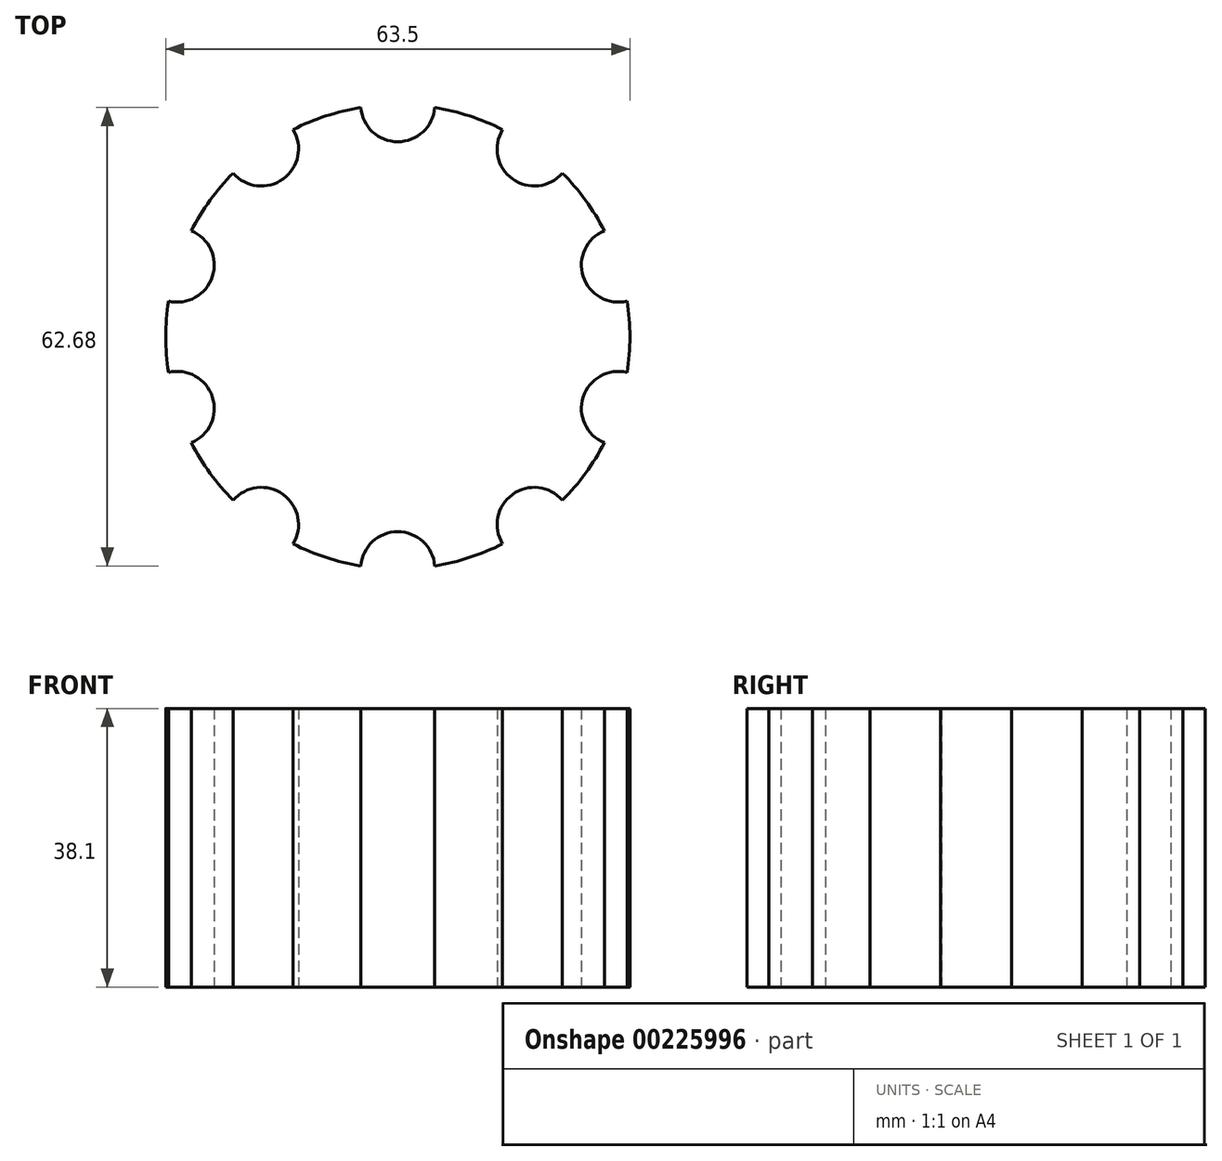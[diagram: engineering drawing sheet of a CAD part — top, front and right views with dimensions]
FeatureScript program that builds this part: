
annotation { "Feature Type Name" : "Feature", "Feature Type Description" : "" }
export const myFeature = defineFeature(function(context is Context, id is Id, definition is map)
    precondition{}
    {
        {
            var Q0;
            Q0=qCreatedBy(makeId("Top.planeOp"),FACE);
            var sketch = newSketch(context, id + "F0", { "sketchPlane" : qUnion([Q0])});
            skCircle(sketch, "E0", {"center": v(0, 0) * mm, "radius": 31.75 * mm});
            skSolve(sketch);
        }
        {
            var Q0;
            Q0=qSketchRegion(id+"F0",true);
            extrude(context, id + "F1", {"entities" : qUnion([Q0]), "depth" : 38.1 * mm});
        }
        {
            var Q0;
            Q0=qCreatedBy(makeId("Top.planeOp"),FACE);
            var sketch = newSketch(context, id + "F2", { "sketchPlane" : qUnion([Q0])});
            skCircle(sketch, "E1", {"center": v(0, 31.75) * mm, "radius": 5.08 * mm});
            skCircle(sketch, "E2.1.0", {"center": v(-18.66, 25.69) * mm, "radius": 5.08 * mm});
            skCircle(sketch, "E2.2.0", {"center": v(-30.2, 9.81) * mm, "radius": 5.08 * mm});
            skCircle(sketch, "E2.3.0", {"center": v(-30.2, -9.81) * mm, "radius": 5.08 * mm});
            skCircle(sketch, "E2.4.0", {"center": v(-18.66, -25.69) * mm, "radius": 5.08 * mm});
            skCircle(sketch, "E2.5.0", {"center": v(0, -31.75) * mm, "radius": 5.08 * mm});
            skCircle(sketch, "E2.6.0", {"center": v(18.66, -25.69) * mm, "radius": 5.08 * mm});
            skCircle(sketch, "E2.7.0", {"center": v(30.2, -9.81) * mm, "radius": 5.08 * mm});
            skCircle(sketch, "E2.8.0", {"center": v(30.2, 9.81) * mm, "radius": 5.08 * mm});
            skCircle(sketch, "E2.9.0", {"center": v(18.66, 25.69) * mm, "radius": 5.08 * mm});
            skPoint(sketch, "E2.center", {"position": v(0, 0) * mm});
            skSolve(sketch);
        }
        {
            var Q0;
            Q0=qSketchRegion(id+"F2",true);
            extrude(context, id + "F3", {"entities" : qUnion([Q0]), "depth" : 50.8 * mm});
        }
        {
            var Q0;
            Q0=makeQuery(id+"F3.opExtrude","SWEPT_BODY",BODY,{"disambiguationData":[OSD([sQuery(id+"F2.wireOp",EDGE,"E2.2.0")])]});
            var Q1;
            Q1=makeQuery(id+"F3.opExtrude","SWEPT_BODY",BODY,{"disambiguationData":[OSD([sQuery(id+"F2.wireOp",EDGE,"E2.3.0")])]});
            var Q2;
            Q2=makeQuery(id+"F3.opExtrude","SWEPT_BODY",BODY,{"disambiguationData":[OSD([sQuery(id+"F2.wireOp",EDGE,"E2.4.0")])]});
            var Q3;
            Q3=makeQuery(id+"F3.opExtrude","SWEPT_BODY",BODY,{"disambiguationData":[OSD([sQuery(id+"F2.wireOp",EDGE,"E2.5.0")])]});
            var Q4;
            Q4=makeQuery(id+"F3.opExtrude","SWEPT_BODY",BODY,{"disambiguationData":[OSD([sQuery(id+"F2.wireOp",EDGE,"E2.6.0")])]});
            var Q5;
            Q5=makeQuery(id+"F3.opExtrude","SWEPT_BODY",BODY,{"disambiguationData":[OSD([sQuery(id+"F2.wireOp",EDGE,"E2.7.0")])]});
            var Q6;
            Q6=makeQuery(id+"F3.opExtrude","SWEPT_BODY",BODY,{"disambiguationData":[OSD([sQuery(id+"F2.wireOp",EDGE,"E2.8.0")])]});
            var Q7;
            Q7=makeQuery(id+"F3.opExtrude","SWEPT_BODY",BODY,{"disambiguationData":[OSD([sQuery(id+"F2.wireOp",EDGE,"E2.9.0")])]});
            var Q8;
            Q8=makeQuery(id+"F3.opExtrude","SWEPT_BODY",BODY,{"disambiguationData":[OSD([sQuery(id+"F2.wireOp",EDGE,"E1")])]});
            var Q9;
            Q9=makeQuery(id+"F3.opExtrude","SWEPT_BODY",BODY,{"disambiguationData":[OSD([sQuery(id+"F2.wireOp",EDGE,"E2.1.0")])]});
            var Q10;
            Q10=makeQuery(id+"F1.opExtrude","SWEPT_BODY",BODY,{"disambiguationData":[OSD([sQuery(id+"F0.wireOp",EDGE,"E0")])]});
            booleanBodies(context, id + "F4", {"operationType" : BooleanOperationType.SUBTRACTION, "tools" : qUnion([Q0, Q1, Q2, Q3, Q4, Q5, Q6, Q7, Q8, Q9]), "targets" : qUnion([Q10])});
        }
    });
